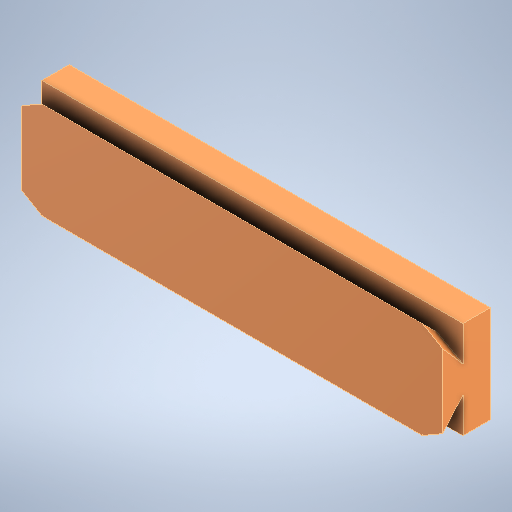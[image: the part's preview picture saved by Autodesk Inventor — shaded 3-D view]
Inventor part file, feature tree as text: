
AUTODESK INVENTOR PART (.ipt)
format: ipt  version: 2025 (Build 290162000, 162)  size: 279,040 bytes
history: native  units: in
note: dims shown in document units (in); Inventor stores cm internally (conversion verified against a paired STEP export)
features: extrude x1, sketch x1
ambient origin geometry x8: Origin, YZ Plane, XZ Plane, XY Plane, X Axis, Y Axis, Z Axis, Center Point
bodies: Solid2 (feature_tree), Solid1 (feature_tree)
feature tree (2):
  extrude  "Extrusion2"  Depth=0.1575in TaperAngle=0.0deg
  sketch  "Sketch1"  dims[d0=0.0022in d3=0.1575in d4=0.0in]
